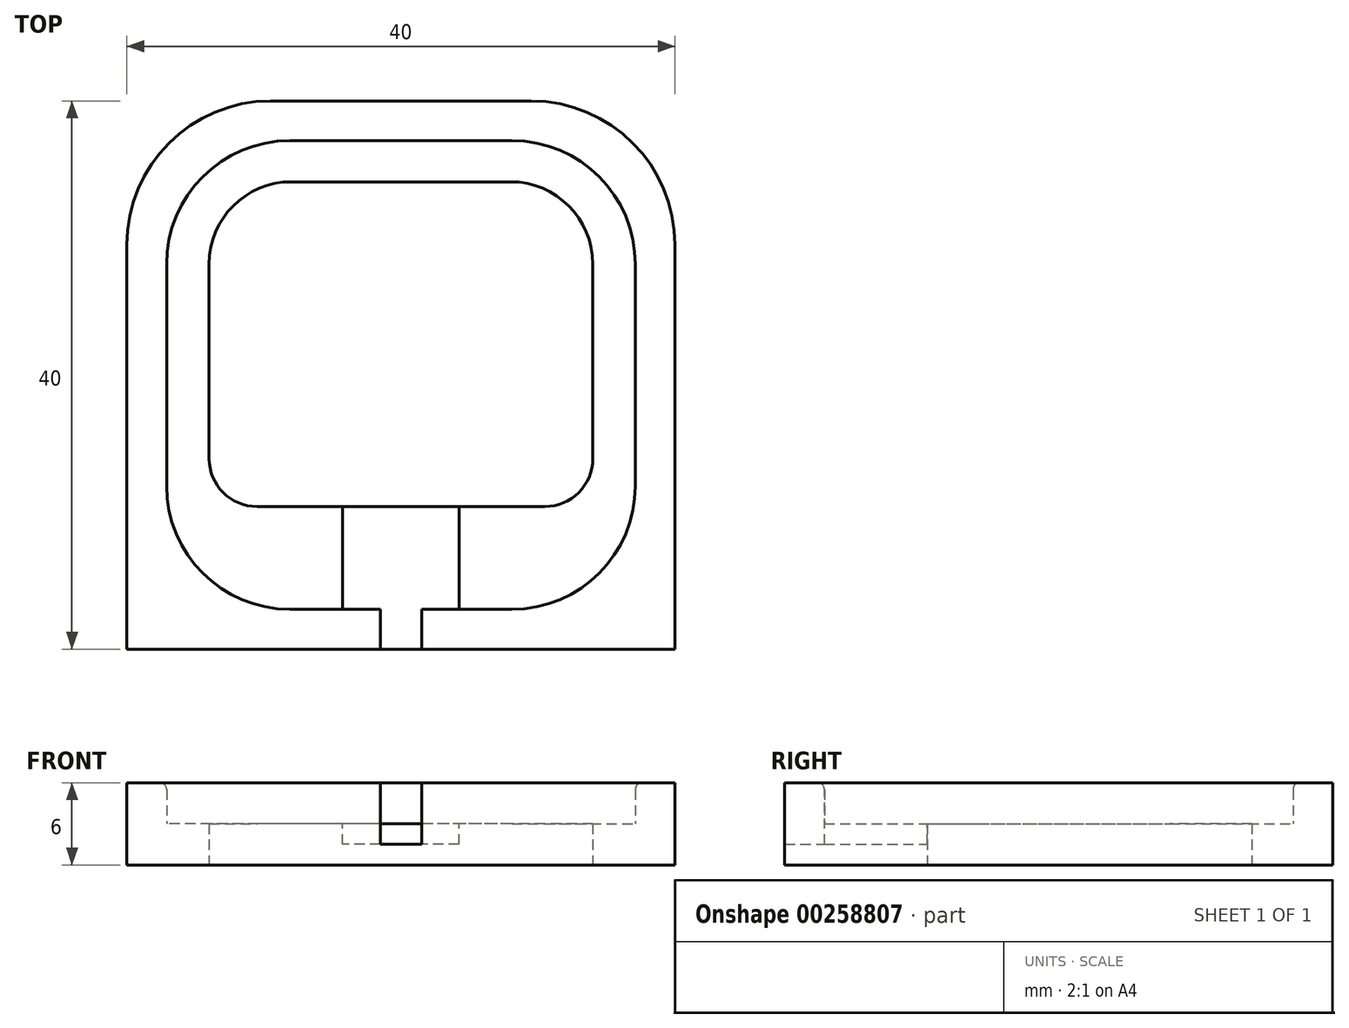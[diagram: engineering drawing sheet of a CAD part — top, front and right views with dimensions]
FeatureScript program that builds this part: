
annotation { "Feature Type Name" : "Feature", "Feature Type Description" : "" }
export const myFeature = defineFeature(function(context is Context, id is Id, definition is map)
    precondition{}
    {
        {
            var Q0;
            Q0=qCreatedBy(makeId("Top.planeOp"),FACE);
            var sketch = newSketch(context, id + "F0", { "sketchPlane" : qUnion([Q0])});
            skLineSegment(sketch, "E0.bottom", {"start": v(8.1, -17.1) * mm, "end": v(-8.1, -17.1) * mm});
            skLineSegment(sketch, "E0.top", {"start": v(8.1, 17.1) * mm, "end": v(-8.1, 17.1) * mm});
            skLineSegment(sketch, "E0.left", {"start": v(17.1, -8.1) * mm, "end": v(17.1, 8.1) * mm});
            skLineSegment(sketch, "E0.right", {"start": v(-17.1, -8.1) * mm, "end": v(-17.1, 8.1) * mm});
            skPoint(sketch, "E0.middle", {"position": v(0, 0) * mm});
            skLineSegment(sketch, "E1.bottom", {"start": v(10.5, -9.6) * mm, "end": v(-10.5, -9.6) * mm});
            skLineSegment(sketch, "E1.top", {"start": v(8, 14.1) * mm, "end": v(-8, 14.1) * mm});
            skLineSegment(sketch, "E2.bottom", {"start": v(20, -20) * mm, "end": v(-20, -20) * mm});
            skLineSegment(sketch, "E2.top", {"start": v(9.5, 20) * mm, "end": v(-9.5, 20) * mm});
            skLineSegment(sketch, "E2.left", {"start": v(20, -20) * mm, "end": v(20, 9.5) * mm});
            skLineSegment(sketch, "E2.right", {"start": v(-20, -20) * mm, "end": v(-20, 9.5) * mm});
            skPoint(sketch, "E3.visualSharp", {"position": v(-17.1, 17.1) * mm});
            skArc(sketch, "E3.filletArc", {"start": v(-8.1, 17.1) * mm, "mid": v(-14.46, 14.46) * mm, "end": v(-17.1, 8.1) * mm});
            skPoint(sketch, "E4.visualSharp", {"position": v(17.1, 17.1) * mm});
            skArc(sketch, "E4.filletArc", {"start": v(17.1, 8.1) * mm, "mid": v(14.46, 14.46) * mm, "end": v(8.1, 17.1) * mm});
            skPoint(sketch, "E5.visualSharp", {"position": v(17.1, -17.1) * mm});
            skArc(sketch, "E5.filletArc", {"start": v(8.1, -17.1) * mm, "mid": v(14.46, -14.46) * mm, "end": v(17.1, -8.1) * mm});
            skPoint(sketch, "E6.visualSharp", {"position": v(-17.1, -17.1) * mm});
            skArc(sketch, "E6.filletArc", {"start": v(-17.1, -8.1) * mm, "mid": v(-14.46, -14.46) * mm, "end": v(-8.1, -17.1) * mm});
            skPoint(sketch, "E7.visualSharp", {"position": v(-14, 14.1) * mm});
            skArc(sketch, "E7.filletArc", {"start": v(-8, 14.1) * mm, "mid": v(-12.24, 12.34) * mm, "end": v(-14, 8.1) * mm});
            skPoint(sketch, "E8.visualSharp", {"position": v(14, 14.1) * mm});
            skArc(sketch, "E8.filletArc", {"start": v(14, 8.1) * mm, "mid": v(12.24, 12.34) * mm, "end": v(8, 14.1) * mm});
            skPoint(sketch, "E9.visualSharp", {"position": v(14, -9.6) * mm});
            skArc(sketch, "E9.filletArc", {"start": v(10.5, -9.6) * mm, "mid": v(12.97, -8.57) * mm, "end": v(14, -6.1) * mm});
            skPoint(sketch, "E10.visualSharp", {"position": v(-14, -14.1) * mm});
            skArc(sketch, "E10.filletArc", {"start": v(-14, -6.1) * mm, "mid": v(-12.97, -8.57) * mm, "end": v(-10.5, -9.6) * mm});
            skPoint(sketch, "E11.visualSharp", {"position": v(-20, 20) * mm});
            skArc(sketch, "E11.filletArc", {"start": v(-9.5, 20) * mm, "mid": v(-16.92, 16.92) * mm, "end": v(-20, 9.5) * mm});
            skPoint(sketch, "E12.visualSharp", {"position": v(20, 20) * mm});
            skArc(sketch, "E12.filletArc", {"start": v(20, 9.5) * mm, "mid": v(16.92, 16.92) * mm, "end": v(9.5, 20) * mm});
            skLineSegment(sketch, "E13", {"start": v(-14, 0) * mm, "end": v(-14, 8.1) * mm});
            skLineSegment(sketch, "E14", {"start": v(14, 0) * mm, "end": v(14, 8.1) * mm});
            skLineSegment(sketch, "E15", {"start": v(-14, -6.1) * mm, "end": v(-14, 0) * mm});
            skLineSegment(sketch, "E16", {"start": v(14, -6.1) * mm, "end": v(14, 0) * mm});
            skLineSegment(sketch, "E17", {"start": v(-14, 0) * mm, "end": v(0, 0) * mm, "construction": true});
            skLineSegment(sketch, "E18", {"start": v(0, 0) * mm, "end": v(14, 0) * mm, "construction": true});
            skSolve(sketch);
        }
        {
            var Q0;
            Q0=makeQuery(id+"F0.imprint","IMPRINT",FACE,{"disambiguationData":[TD([[makeQuery(id+"F0.imprint","IMPRINT",EDGE,{"derivedFrom":sQuery(id+"F0.wireOp",EDGE,"E0.bottom")}),-1.0]])]});
            extrude(context, id + "F1", {"entities" : qUnion([Q0]), "depth" : 3 * mm});
        }
        {
            var Q0;
            Q0=makeQuery(id+"F0.imprint","IMPRINT",FACE,{"disambiguationData":[TD([[makeQuery(id+"F0.imprint","IMPRINT",EDGE,{"derivedFrom":sQuery(id+"F0.wireOp",EDGE,"E0.bottom")}),1.0]])]});
            extrude(context, id + "F2", {"entities" : qUnion([Q0]), "operationType" : NewBodyOperationType.ADD, "depth" : 6 * mm});
        }
        {
            var Q0;
            Q0=makeQuery(id+"F1.opExtrude","CAP_FACE",FACE,{"disambiguationData":[OSD([sQuery(id+"F0.wireOp",EDGE,"E0.bottom"),sQuery(id+"F0.wireOp",EDGE,"E0.top"),sQuery(id+"F0.wireOp",EDGE,"E0.left"),sQuery(id+"F0.wireOp",EDGE,"E0.right"),sQuery(id+"F0.wireOp",EDGE,"E1.bottom"),sQuery(id+"F0.wireOp",EDGE,"E1.top"),sQuery(id+"F0.wireOp",EDGE,"E1.left"),sQuery(id+"F0.wireOp",EDGE,"E1.right"),sQuery(id+"F0.wireOp",EDGE,"E3.filletArc"),sQuery(id+"F0.wireOp",EDGE,"E4.filletArc"),sQuery(id+"F0.wireOp",EDGE,"E5.filletArc"),sQuery(id+"F0.wireOp",EDGE,"E6.filletArc"),sQuery(id+"F0.wireOp",EDGE,"E7.filletArc"),sQuery(id+"F0.wireOp",EDGE,"E8.filletArc"),sQuery(id+"F0.wireOp",EDGE,"E9.filletArc"),sQuery(id+"F0.wireOp",EDGE,"E10.filletArc")])],"isStart":false});
            var sketch = newSketch(context, id + "F3", { "sketchPlane" : qUnion([Q0])});
            skLineSegment(sketch, "E19.bottom", {"start": v(4.25, -17.1) * mm, "end": v(-4.25, -17.1) * mm});
            skLineSegment(sketch, "E19.top", {"start": v(4.25, -9.6) * mm, "end": v(-4.25, -9.6) * mm});
            skLineSegment(sketch, "E19.left", {"start": v(4.25, -17.1) * mm, "end": v(4.25, -9.6) * mm});
            skLineSegment(sketch, "E19.right", {"start": v(-4.25, -17.1) * mm, "end": v(-4.25, -9.6) * mm});
            skPoint(sketch, "E19.middle", {"position": v(0, -13.35) * mm});
            skLineSegment(sketch, "E20.bottom", {"start": v(1.5, -20) * mm, "end": v(-1.5, -20) * mm});
            skLineSegment(sketch, "E20.top", {"start": v(1.5, -17.1) * mm, "end": v(-1.5, -17.1) * mm});
            skLineSegment(sketch, "E20.left", {"start": v(1.5, -20) * mm, "end": v(1.5, -17.1) * mm});
            skLineSegment(sketch, "E20.right", {"start": v(-1.5, -20) * mm, "end": v(-1.5, -17.1) * mm});
            skPoint(sketch, "E20.middle", {"position": v(0, -18.55) * mm});
            skPoint(sketch, "E20.middle.positionSnap0", {"position": v(0, -17.1) * mm});
            skPoint(sketch, "E20.centerSnap0", {"position": v(0, -17.1) * mm});
            skSolve(sketch);
        }
        {
            var Q0;
            Q0 = qSketchRegion(id + "F3", true);
            var Q1;
            Q1=makeQuery(id+"F2.opExtrude","CAP_FACE",FACE,{"disambiguationData":[OSD([sQuery(id+"F0.wireOp",EDGE,"E0.bottom"),sQuery(id+"F0.wireOp",EDGE,"E0.top"),sQuery(id+"F0.wireOp",EDGE,"E0.left"),sQuery(id+"F0.wireOp",EDGE,"E0.right"),sQuery(id+"F0.wireOp",EDGE,"E2.bottom"),sQuery(id+"F0.wireOp",EDGE,"E2.top"),sQuery(id+"F0.wireOp",EDGE,"E2.left"),sQuery(id+"F0.wireOp",EDGE,"E2.right"),sQuery(id+"F0.wireOp",EDGE,"E3.filletArc"),sQuery(id+"F0.wireOp",EDGE,"E4.filletArc"),sQuery(id+"F0.wireOp",EDGE,"E5.filletArc"),sQuery(id+"F0.wireOp",EDGE,"E6.filletArc")])],"isStart":false});
            extrude(context, id + "F4", {"entities" : qUnion([Q0]), "operationType" : NewBodyOperationType.REMOVE, "oppositeDirection" : true, "depth" : 1.5 * mm});
        }
        {
            var Q0;
            Q0=makeQuery(id+"F3.imprint","IMPRINT",FACE,{"disambiguationData":[TD([[makeQuery(id+"F3.imprint","IMPRINT",EDGE,{"derivedFrom":sQuery(id+"F3.wireOp",EDGE,"E20.bottom")}),-1.0]])]});
            extrude(context, id + "F5", {"entities" : qUnion([Q0]), "operationType" : NewBodyOperationType.REMOVE, "endBound" : BoundingType.UP_TO_NEXT, "depth" : 25 * mm});
        }
        {
            var Q0;
            Q0=makeQuery(id+"F2.opExtrude","CAP_EDGE",EDGE,{"disambiguationData":[OSD([sQuery(id+"F0.wireOp",EDGE,"E3.filletArc")])],"isStart":false});
            var Q1;
            Q1=makeQuery(id+"F5.boolean.opBoolean","COPY",EDGE,{"derivedFrom":makeQuery(id+"F5.opExtrude","CAP_EDGE",EDGE,{"disambiguationData":[OSD([sQuery(id+"F3.wireOp",EDGE,"E20.right")])],"isStart":false})});
            var Q2;
            Q2=makeQuery(id+"F5.boolean.opBoolean","COPY",EDGE,{"derivedFrom":makeQuery(id+"F5.opExtrude","CAP_EDGE",EDGE,{"disambiguationData":[OSD([sQuery(id+"F3.wireOp",EDGE,"E20.left")])],"isStart":false})});
            var Q3;
            Q3=makeQuery(id+"F4.boolean.opBoolean","COPY",EDGE,{"derivedFrom":makeQuery(id+"F4.opExtrude","CAP_EDGE",EDGE,{"disambiguationData":[OSD([sQuery(id+"F3.wireOp",EDGE,"E19.right")])],"isStart":true})});
            var Q4;
            Q4=makeQuery(id+"F4.boolean.opBoolean","COPY",EDGE,{"derivedFrom":makeQuery(id+"F4.opExtrude","CAP_EDGE",EDGE,{"disambiguationData":[OSD([sQuery(id+"F3.wireOp",EDGE,"E19.left")])],"isStart":true})});
            fillet(context, id + "F6", {"entities" : qUnion([Q0, Q1, Q2, Q3, Q4]), "radius" : 0.5 * mm, "tangentPropagation" : true, "allowEdgeOverflow" : false});
        }
    });
